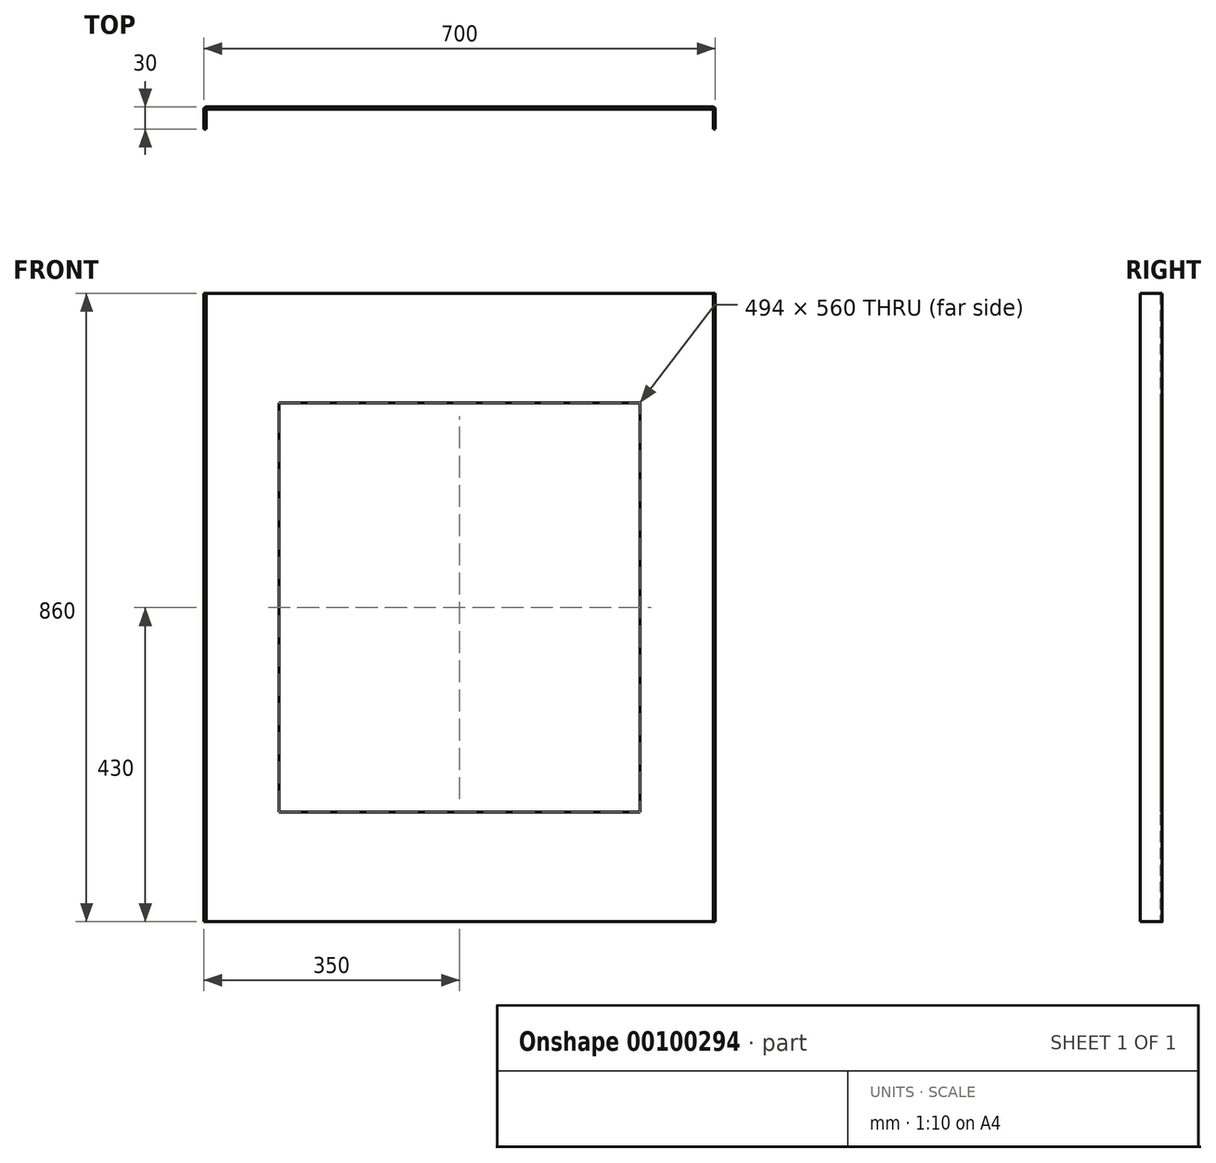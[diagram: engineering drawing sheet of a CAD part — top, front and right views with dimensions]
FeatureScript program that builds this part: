
annotation { "Feature Type Name" : "Feature", "Feature Type Description" : "" }
export const myFeature = defineFeature(function(context is Context, id is Id, definition is map)
    precondition{}
    {
        {
            var Q0;
            Q0=qCreatedBy(makeId("Top.planeOp"),FACE);
            var sketch = newSketch(context, id + "F0", { "sketchPlane" : qUnion([Q0])});
            skLineSegment(sketch, "E0", {"start": v(0, 0) * mm, "end": v(0, 3) * mm, "construction": true});
            skLineSegment(sketch, "E1", {"start": v(0, 3) * mm, "end": v(-347, 3) * mm});
            skLineSegment(sketch, "E2", {"start": v(0, 3) * mm, "end": v(347, 3) * mm});
            skLineSegment(sketch, "E3", {"start": v(350, 0) * mm, "end": v(350, -27) * mm});
            skLineSegment(sketch, "E4", {"start": v(350, -27) * mm, "end": v(347, -27) * mm});
            skLineSegment(sketch, "E5", {"start": v(347, -27) * mm, "end": v(347, -1.5) * mm});
            skLineSegment(sketch, "E6.MirrorCS", {"start": v(-350, -27) * mm, "end": v(-347, -27) * mm});
            skLineSegment(sketch, "E7.MirrorCS", {"start": v(-347, -27) * mm, "end": v(-347, -1.5) * mm});
            skLineSegment(sketch, "E8.MirrorCS", {"start": v(-350, 0) * mm, "end": v(-350, -27) * mm});
            skPoint(sketch, "E9.visualSharp", {"position": v(-347, 0) * mm});
            skArc(sketch, "E9.filletArc", {"start": v(-345.5, 0) * mm, "mid": v(-346.56, -0.44) * mm, "end": v(-347, -1.5) * mm});
            skPoint(sketch, "E10.visualSharp", {"position": v(-350, 3) * mm});
            skArc(sketch, "E10.filletArc", {"start": v(-347, 3) * mm, "mid": v(-349.12, 2.12) * mm, "end": v(-350, 0) * mm});
            skPoint(sketch, "E11.visualSharp", {"position": v(350, 3) * mm});
            skArc(sketch, "E11.filletArc", {"start": v(350, 0) * mm, "mid": v(349.12, 2.12) * mm, "end": v(347, 3) * mm});
            skArc(sketch, "E12.filletArc", {"start": v(347, -1.5) * mm, "mid": v(346.56, -0.44) * mm, "end": v(345.5, 0) * mm});
            skLineSegment(sketch, "E13", {"start": v(350, -27) * mm, "end": v(-350, -27) * mm, "construction": true});
            skLineSegment(sketch, "E14", {"start": v(-345.5, 0) * mm, "end": v(345.5, 0) * mm});
            skSolve(sketch);
        }
        {
            var Q0;
            Q0=makeQuery(id+"F0.imprint","IMPRINT",FACE,{"disambiguationData":[TD([[makeQuery(id+"F0.imprint","IMPRINT",EDGE,{"derivedFrom":sQuery(id+"F0.wireOp",EDGE,"E1")}),1.0]])]});
            extrude(context, id + "F1", {"entities" : qUnion([Q0]), "depth" : 860 * mm});
        }
        {
            var Q0;
            Q0=makeQuery(id+"F1.opExtrude","SWEPT_FACE",FACE,{"disambiguationData":[OSD([sQuery(id+"F0.wireOp",EDGE,"E14")])]});
            var sketch = newSketch(context, id + "F2", { "sketchPlane" : qUnion([Q0])});
            skLineSegment(sketch, "E15.bottom", {"start": v(-247, 710) * mm, "end": v(247, 710) * mm});
            skLineSegment(sketch, "E15.top", {"start": v(-247, 150) * mm, "end": v(247, 150) * mm});
            skLineSegment(sketch, "E15.left", {"start": v(-247, 710) * mm, "end": v(-247, 150) * mm});
            skLineSegment(sketch, "E15.right", {"start": v(247, 710) * mm, "end": v(247, 150) * mm});
            skSolve(sketch);
        }
        {
            var Q0;
            Q0 = qSketchRegion(id + "F2", true);
            extrude(context, id + "F3", {"entities" : qUnion([Q0]), "operationType" : NewBodyOperationType.REMOVE, "oppositeDirection" : true, "depth" : 25 * mm});
        }
    });
